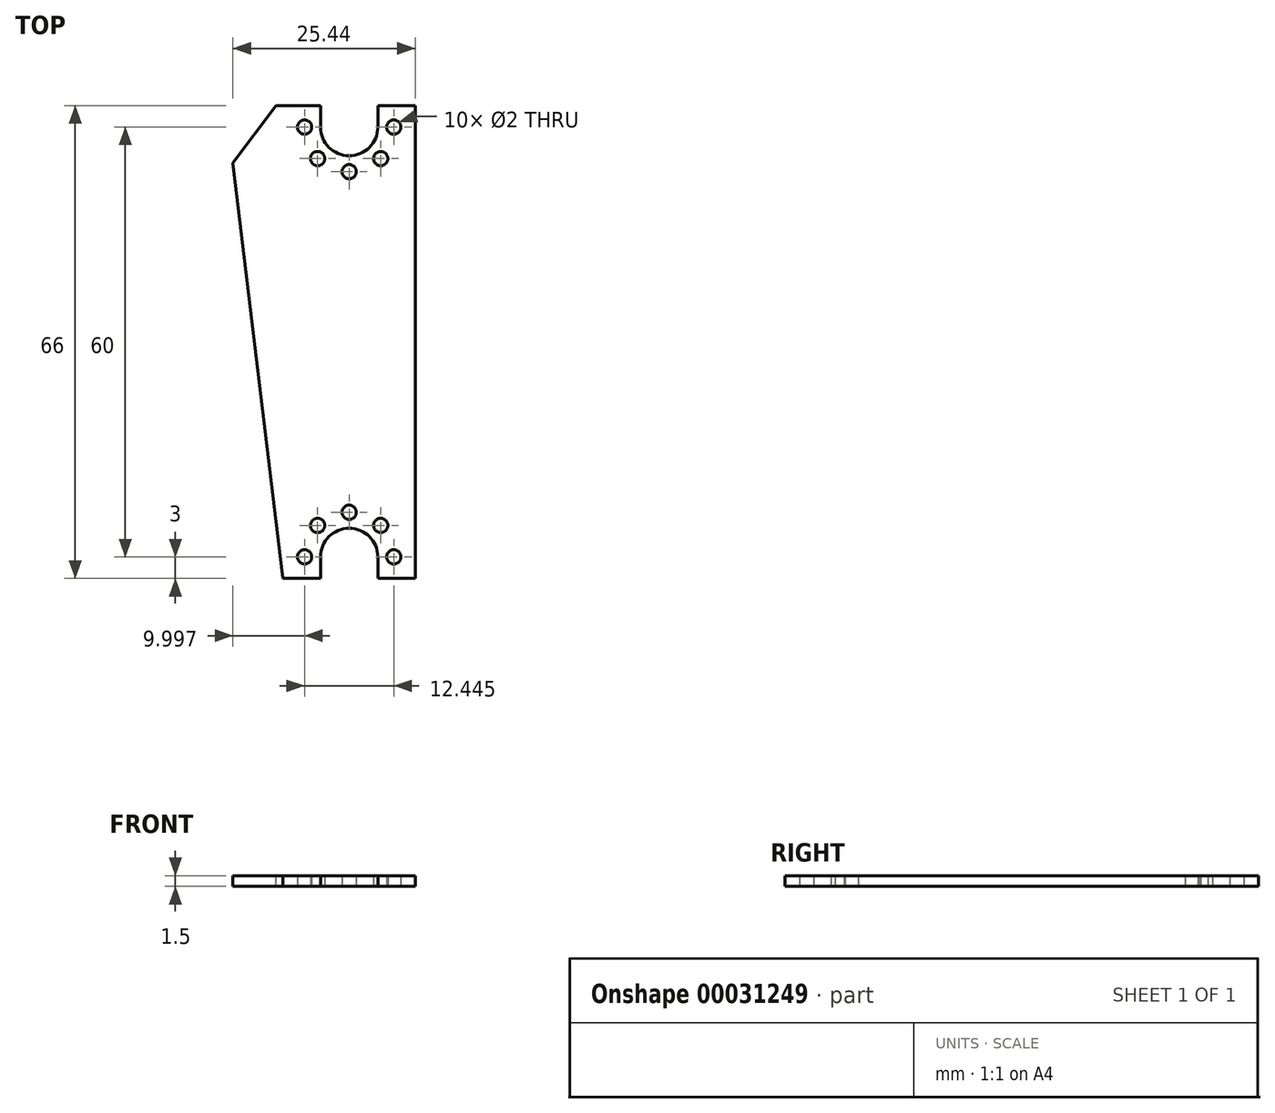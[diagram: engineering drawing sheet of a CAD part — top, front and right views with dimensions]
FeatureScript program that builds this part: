
annotation { "Feature Type Name" : "Feature", "Feature Type Description" : "" }
export const myFeature = defineFeature(function(context is Context, id is Id, definition is map)
    precondition{}
    {
        {
            var Q0;
            Q0=qCreatedBy(makeId("Top.planeOp"),FACE);
            var sketch = newSketch(context, id + "F0", { "sketchPlane" : qUnion([Q0])});
            skLineSegment(sketch, "E0.bottom", {"start": v(-16.22, 33) * mm, "end": v(-4, 33) * mm});
            skLineSegment(sketch, "E0.top", {"start": v(-16.22, -33) * mm, "end": v(-4, -33) * mm});
            skLineSegment(sketch, "E0.left", {"start": v(-16.22, 33) * mm, "end": v(-16.22, -33) * mm});
            skLineSegment(sketch, "E0.right", {"start": v(16.22, 33) * mm, "end": v(16.22, -33) * mm});
            skPoint(sketch, "E0.middle", {"position": v(0, 0) * mm});
            skArc(sketch, "E1", {"start": v(-4, 30) * mm, "mid": v(0, 26) * mm, "end": v(4, 30) * mm});
            skLineSegment(sketch, "E2.bottom", {"start": v(4.4, 25.6) * mm, "end": v(-4.4, 25.6) * mm, "construction": true});
            skLineSegment(sketch, "E2.top", {"start": v(4.4, 34.4) * mm, "end": v(-4.4, 34.4) * mm, "construction": true});
            skLineSegment(sketch, "E2.left", {"start": v(4.4, 25.6) * mm, "end": v(4.4, 34.4) * mm, "construction": true});
            skLineSegment(sketch, "E2.right", {"start": v(-4.4, 25.6) * mm, "end": v(-4.4, 34.4) * mm, "construction": true});
            skCircle(sketch, "E3", {"center": v(4.4, 25.6) * mm, "radius": 1 * mm});
            skCircle(sketch, "E4.1.0", {"center": v(6.22, 30) * mm, "radius": 1 * mm});
            skCircle(sketch, "E4.5.0", {"center": v(-6.22, 30) * mm, "radius": 1 * mm});
            skCircle(sketch, "E4.6.0", {"center": v(-4.4, 25.6) * mm, "radius": 1 * mm});
            skCircle(sketch, "E4.7.0", {"center": v(0, 23.78) * mm, "radius": 1 * mm});
            skLineSegment(sketch, "E5", {"start": v(-4, 30) * mm, "end": v(-4, 33) * mm});
            skLineSegment(sketch, "E6", {"start": v(4, 30) * mm, "end": v(4, 33) * mm});
            skLineSegment(sketch, "E7.trimOffspring", {"start": v(4, 33) * mm, "end": v(16.22, 33) * mm});
            skPoint(sketch, "E8.MirrorP", {"position": v(0, -30) * mm});
            skLineSegment(sketch, "E9.MirrorCS", {"start": v(-4, -30) * mm, "end": v(-4, -33) * mm});
            skCircle(sketch, "E10.MirrorC", {"center": v(0, -23.78) * mm, "radius": 1 * mm});
            skLineSegment(sketch, "E11.MirrorCS", {"start": v(4, -30) * mm, "end": v(4, -33) * mm});
            skCircle(sketch, "E12.MirrorC", {"center": v(-4.4, -25.6) * mm, "radius": 1 * mm});
            skCircle(sketch, "E13.MirrorC", {"center": v(6.22, -30) * mm, "radius": 1 * mm});
            skCircle(sketch, "E14.MirrorC", {"center": v(-6.22, -30) * mm, "radius": 1 * mm});
            skArc(sketch, "E15.MirrorCS", {"start": v(-4, -30) * mm, "mid": v(0, -26) * mm, "end": v(4, -30) * mm});
            skCircle(sketch, "E16.MirrorC", {"center": v(4.4, -25.6) * mm, "radius": 1 * mm});
            skLineSegment(sketch, "E17.trimOffspring", {"start": v(4, -33) * mm, "end": v(16.22, -33) * mm});
            skSolve(sketch);
        }
        {
            var Q0;
            Q0=qSketchRegion(id+"F0",true);
            extrude(context, id + "F1", {"entities" : qUnion([Q0]), "depth" : 1.5 * mm});
        }
        {
            var Q0;
            Q0=makeQuery(id+"F1.opExtrude","CAP_FACE",FACE,{"disambiguationData":[OSD([sQuery(id+"F0.wireOp",EDGE,"E0.bottom"),sQuery(id+"F0.wireOp",EDGE,"E0.top"),sQuery(id+"F0.wireOp",EDGE,"E0.left"),sQuery(id+"F0.wireOp",EDGE,"E0.right"),sQuery(id+"F0.wireOp",EDGE,"E1"),sQuery(id+"F0.wireOp",EDGE,"E3"),sQuery(id+"F0.wireOp",EDGE,"E4.1.0"),sQuery(id+"F0.wireOp",EDGE,"E4.5.0"),sQuery(id+"F0.wireOp",EDGE,"E4.6.0"),sQuery(id+"F0.wireOp",EDGE,"E4.7.0"),sQuery(id+"F0.wireOp",EDGE,"E5"),sQuery(id+"F0.wireOp",EDGE,"E6"),sQuery(id+"F0.wireOp",EDGE,"E7.trimOffspring"),sQuery(id+"F0.wireOp",EDGE,"E9.MirrorCS"),sQuery(id+"F0.wireOp",EDGE,"E10.MirrorC"),sQuery(id+"F0.wireOp",EDGE,"E11.MirrorCS"),sQuery(id+"F0.wireOp",EDGE,"E12.MirrorC"),sQuery(id+"F0.wireOp",EDGE,"E13.MirrorC"),sQuery(id+"F0.wireOp",EDGE,"E14.MirrorC"),sQuery(id+"F0.wireOp",EDGE,"E15.MirrorCS"),sQuery(id+"F0.wireOp",EDGE,"E16.MirrorC"),sQuery(id+"F0.wireOp",EDGE,"E17.trimOffspring")])],"isStart":false});
            var sketch = newSketch(context, id + "F2", { "sketchPlane" : qUnion([Q0])});
            skPoint(sketch, "E18", {"position": v(-6.22, 30) * mm});
            skPoint(sketch, "E19", {"position": v(6.22, 30) * mm});
            skLineSegment(sketch, "E20", {"start": v(9.22, 33) * mm, "end": v(9.22, -33) * mm});
            skLineSegment(sketch, "E21", {"start": v(-10.22, 33) * mm, "end": v(-16.22, 25) * mm});
            skLineSegment(sketch, "E22", {"start": v(-16.22, 25) * mm, "end": v(-9.22, -33) * mm});
            skPoint(sketch, "E23", {"position": v(-6.22, -30) * mm});
            skSolve(sketch);
        }
        {
            var Q0;
            {var subQ0=sQuery(id+"F2.wireOp",EDGE,"E21");Q0=makeQuery(id+"F2.imprint","IMPRINT",FACE,{"disambiguationData":[TD([[makeQuery(id+"F2.imprint","IMPRINT",EDGE,{"derivedFrom":subQ0}),-1.0]])]});}
            var Q1;
            {var subQ0=sQuery(id+"F2.wireOp",EDGE,"E22");Q1=makeQuery(id+"F2.imprint","IMPRINT",FACE,{"disambiguationData":[TD([[makeQuery(id+"F2.imprint","IMPRINT",EDGE,{"derivedFrom":subQ0}),-1.0]])]});}
            var Q2;
            {var subQ0=sQuery(id+"F2.wireOp",EDGE,"E20");Q2=makeQuery(id+"F2.imprint","IMPRINT",FACE,{"disambiguationData":[TD([[makeQuery(id+"F2.imprint","IMPRINT",EDGE,{"derivedFrom":subQ0}),1.0]])]});}
            extrude(context, id + "F3", {"entities" : qUnion([Q0, Q1, Q2]), "operationType" : NewBodyOperationType.REMOVE, "endBound" : BoundingType.UP_TO_NEXT, "oppositeDirection" : true, "depth" : 25 * mm});
        }
    });
